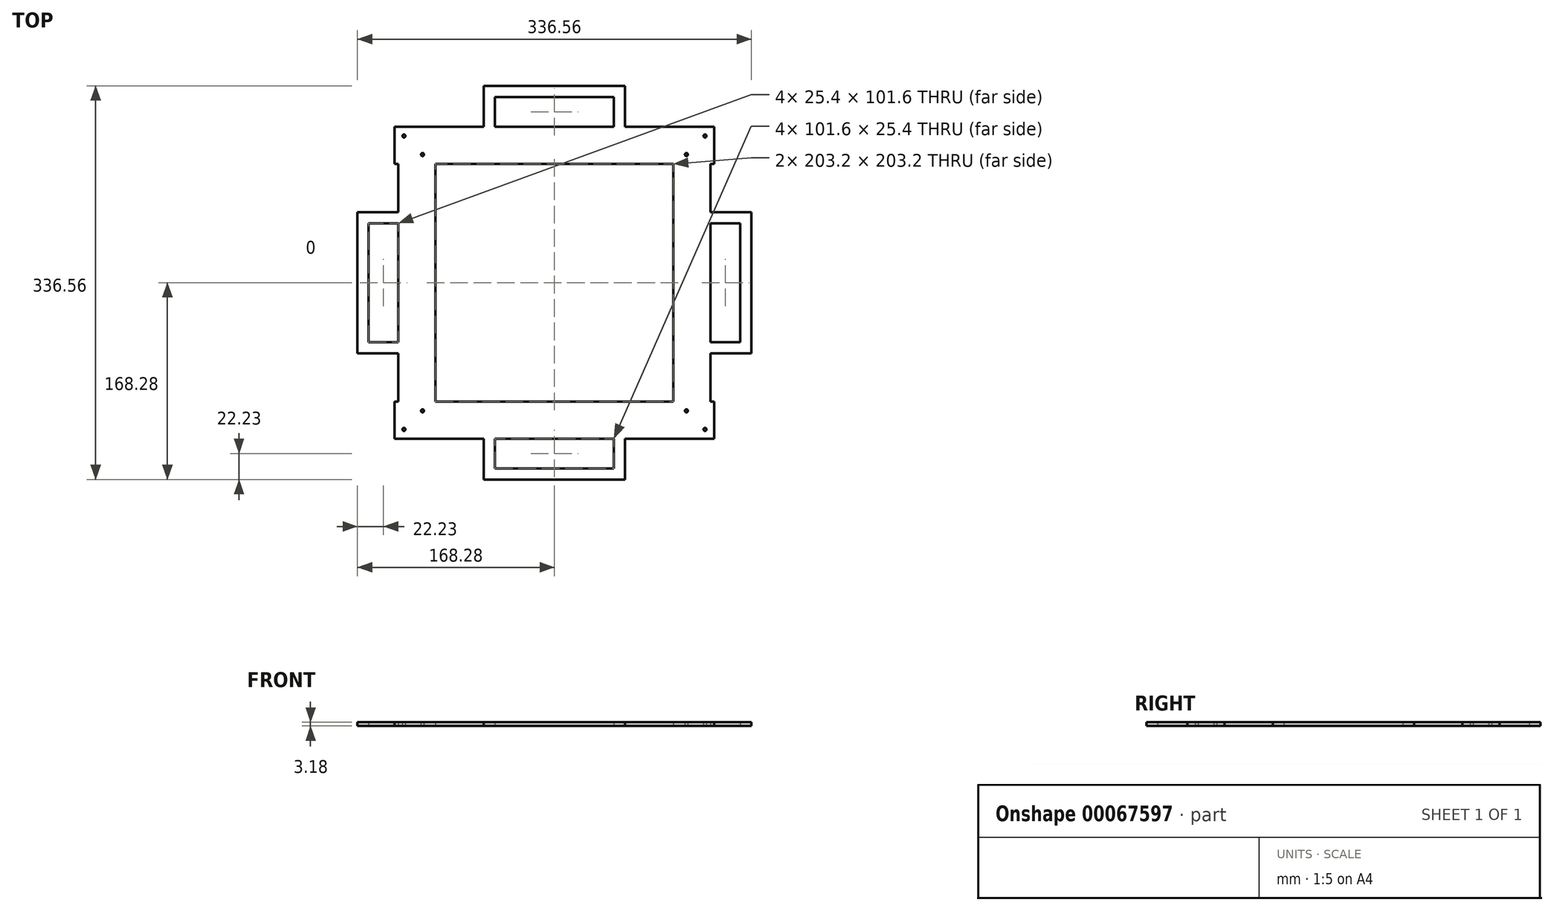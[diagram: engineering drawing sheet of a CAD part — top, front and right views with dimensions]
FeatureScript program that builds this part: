
annotation { "Feature Type Name" : "Feature", "Feature Type Description" : "" }
export const myFeature = defineFeature(function(context is Context, id is Id, definition is map)
    precondition{}
    {
        {
            var Q0;
            Q0=qCreatedBy(makeId("Top.planeOp"),FACE);
            var sketch = newSketch(context, id + "F0", { "sketchPlane" : qUnion([Q0])});
            skLineSegment(sketch, "E0.rect.bottom", {"start": v(101.6, 101.6) * mm, "end": v(-101.6, 101.6) * mm});
            skLineSegment(sketch, "E0.rect.top", {"start": v(101.6, -101.6) * mm, "end": v(-101.6, -101.6) * mm});
            skLineSegment(sketch, "E0.rect.left", {"start": v(101.6, 101.6) * mm, "end": v(101.6, -101.6) * mm});
            skLineSegment(sketch, "E0.rect.right", {"start": v(-101.6, 101.6) * mm, "end": v(-101.6, -101.6) * mm});
            skPoint(sketch, "E0.rect.middle", {"position": v(0, 0) * mm});
            skLineSegment(sketch, "E1", {"start": v(-101.6, 101.6) * mm, "end": v(-104.78, 101.6) * mm});
            skLineSegment(sketch, "E2", {"start": v(101.6, 101.6) * mm, "end": v(104.78, 101.6) * mm});
            skLineSegment(sketch, "E3.0", {"start": v(-133.35, 101.6) * mm, "end": v(-133.35, -101.6) * mm});
            skLineSegment(sketch, "E4", {"start": v(0, 101.6) * mm, "end": v(0, -101.6) * mm});
            skLineSegment(sketch, "E5.0", {"start": v(101.6, 133.35) * mm, "end": v(104.78, 133.35) * mm});
            skLineSegment(sketch, "E5.2", {"start": v(-101.6, 133.35) * mm, "end": v(-104.78, 133.35) * mm});
            skLineSegment(sketch, "E6", {"start": v(101.6, 0) * mm, "end": v(-101.6, 0) * mm});
            skLineSegment(sketch, "E7.bottom", {"start": v(-133.35, 101.6) * mm, "end": v(-136.53, 101.6) * mm});
            skLineSegment(sketch, "E7.top", {"start": v(-104.78, 133.35) * mm, "end": v(-136.53, 133.35) * mm});
            skLineSegment(sketch, "E7.left", {"start": v(-104.78, 101.6) * mm, "end": v(-104.78, 133.35) * mm});
            skLineSegment(sketch, "E7.right", {"start": v(-136.53, 101.6) * mm, "end": v(-136.53, 133.35) * mm});
            skLineSegment(sketch, "E8", {"start": v(-104.78, 101.6) * mm, "end": v(-120.65, 117.48) * mm});
            skLineSegment(sketch, "E9", {"start": v(-120.65, 117.48) * mm, "end": v(-136.53, 133.35) * mm});
            skCircle(sketch, "E10", {"center": v(-128.59, 125.41) * mm, "radius": 1.26 * mm});
            skCircle(sketch, "E11", {"center": v(-112.71, 109.54) * mm, "radius": 1.26 * mm});
            skLineSegment(sketch, "E12.MirrorCS", {"start": v(133.35, 101.6) * mm, "end": v(136.53, 101.6) * mm});
            skLineSegment(sketch, "E13.MirrorCS", {"start": v(136.53, 101.6) * mm, "end": v(136.53, 133.35) * mm});
            skLineSegment(sketch, "E14.MirrorCS", {"start": v(104.78, 133.35) * mm, "end": v(136.53, 133.35) * mm});
            skCircle(sketch, "E15.MirrorC", {"center": v(112.71, -109.54) * mm, "radius": 1.26 * mm});
            skCircle(sketch, "E16.MirrorC", {"center": v(128.59, -125.41) * mm, "radius": 1.26 * mm});
            skLineSegment(sketch, "E17.MirrorCS", {"start": v(136.53, -101.6) * mm, "end": v(136.53, -133.35) * mm});
            skLineSegment(sketch, "E18.MirrorCS", {"start": v(133.35, -101.6) * mm, "end": v(136.53, -101.6) * mm});
            skLineSegment(sketch, "E19.MirrorCS", {"start": v(-133.35, -101.6) * mm, "end": v(-136.53, -101.6) * mm});
            skLineSegment(sketch, "E20.MirrorCS", {"start": v(-136.53, -101.6) * mm, "end": v(-136.53, -133.35) * mm});
            skLineSegment(sketch, "E21", {"start": v(101.6, 133.35) * mm, "end": v(-101.6, 133.35) * mm});
            skLineSegment(sketch, "E22", {"start": v(133.35, 101.6) * mm, "end": v(133.35, -101.6) * mm});
            skLineSegment(sketch, "E23", {"start": v(136.53, -133.35) * mm, "end": v(-136.53, -133.35) * mm});
            skLineSegment(sketch, "E24", {"start": v(0, 133.35) * mm, "end": v(0, 158.75) * mm});
            skLineSegment(sketch, "E25", {"start": v(-50.8, 158.75) * mm, "end": v(0, 158.75) * mm});
            skLineSegment(sketch, "E26", {"start": v(0, 158.75) * mm, "end": v(50.8, 158.75) * mm});
            skLineSegment(sketch, "E27", {"start": v(50.8, 158.75) * mm, "end": v(50.8, 133.35) * mm});
            skLineSegment(sketch, "E28", {"start": v(-50.8, 158.75) * mm, "end": v(-50.8, 133.35) * mm});
            skLineSegment(sketch, "E29.0", {"start": v(-60.33, 168.28) * mm, "end": v(-60.33, 133.35) * mm});
            skLineSegment(sketch, "E29.1", {"start": v(-60.33, 168.28) * mm, "end": v(0, 168.28) * mm});
            skLineSegment(sketch, "E29.2", {"start": v(0, 168.28) * mm, "end": v(60.32, 168.28) * mm});
            skLineSegment(sketch, "E29.3", {"start": v(60.32, 168.28) * mm, "end": v(60.32, 133.35) * mm});
            skLineSegment(sketch, "E30", {"start": v(133.35, 0) * mm, "end": v(158.75, 0) * mm});
            skPoint(sketch, "E30.endSnap0", {"position": v(133.35, 0) * mm});
            skLineSegment(sketch, "E31", {"start": v(158.75, 0) * mm, "end": v(158.75, 50.8) * mm});
            skLineSegment(sketch, "E32", {"start": v(158.75, 50.8) * mm, "end": v(133.35, 50.8) * mm});
            skLineSegment(sketch, "E33.0", {"start": v(168.28, 60.33) * mm, "end": v(133.35, 60.33) * mm});
            skLineSegment(sketch, "E33.1", {"start": v(168.28, 0) * mm, "end": v(168.28, 60.33) * mm});
            skLineSegment(sketch, "E34.MirrorCS", {"start": v(158.75, -50.8) * mm, "end": v(133.35, -50.8) * mm});
            skLineSegment(sketch, "E35.MirrorCS", {"start": v(168.28, -60.33) * mm, "end": v(133.35, -60.33) * mm});
            skLineSegment(sketch, "E36.MirrorCS", {"start": v(168.28, 0) * mm, "end": v(168.28, -60.33) * mm});
            skLineSegment(sketch, "E37.MirrorCS", {"start": v(158.75, 0) * mm, "end": v(158.75, -50.8) * mm});
            skLineSegment(sketch, "E38.MirrorCS", {"start": v(-50.8, -158.75) * mm, "end": v(0, -158.75) * mm});
            skLineSegment(sketch, "E39.MirrorCS", {"start": v(0, -158.75) * mm, "end": v(50.8, -158.75) * mm});
            skLineSegment(sketch, "E40.MirrorCS", {"start": v(50.8, -158.75) * mm, "end": v(50.8, -133.35) * mm});
            skLineSegment(sketch, "E41.MirrorCS", {"start": v(60.32, -168.28) * mm, "end": v(60.32, -133.35) * mm});
            skLineSegment(sketch, "E42.MirrorCS", {"start": v(0, -168.28) * mm, "end": v(60.32, -168.28) * mm});
            skLineSegment(sketch, "E43.MirrorCS", {"start": v(-60.33, -168.28) * mm, "end": v(0, -168.28) * mm});
            skLineSegment(sketch, "E44.MirrorCS", {"start": v(-60.33, -168.28) * mm, "end": v(-60.33, -133.35) * mm});
            skLineSegment(sketch, "E45.MirrorCS", {"start": v(-50.8, -158.75) * mm, "end": v(-50.8, -133.35) * mm});
            skLineSegment(sketch, "E46.MirrorCS", {"start": v(0, -101.6) * mm, "end": v(0, 101.6) * mm});
            skLineSegment(sketch, "E47.MirrorCS", {"start": v(-168.28, 60.33) * mm, "end": v(-133.35, 60.33) * mm});
            skLineSegment(sketch, "E48.MirrorCS", {"start": v(-158.75, 50.8) * mm, "end": v(-133.35, 50.8) * mm});
            skLineSegment(sketch, "E49.MirrorCS", {"start": v(-158.75, 0) * mm, "end": v(-158.75, 50.8) * mm});
            skLineSegment(sketch, "E50.MirrorCS", {"start": v(-168.28, 0) * mm, "end": v(-168.28, 60.33) * mm});
            skLineSegment(sketch, "E51.MirrorCS", {"start": v(-158.75, 0) * mm, "end": v(-158.75, -50.8) * mm});
            skLineSegment(sketch, "E52.MirrorCS", {"start": v(-168.28, 0) * mm, "end": v(-168.28, -60.33) * mm});
            skLineSegment(sketch, "E53.MirrorCS", {"start": v(-168.28, -60.33) * mm, "end": v(-133.35, -60.33) * mm});
            skLineSegment(sketch, "E54.MirrorCS", {"start": v(-158.75, -50.8) * mm, "end": v(-133.35, -50.8) * mm});
            skCircle(sketch, "E55.MirrorC", {"center": v(112.71, 109.54) * mm, "radius": 1.26 * mm});
            skCircle(sketch, "E56.MirrorC", {"center": v(128.59, 125.41) * mm, "radius": 1.26 * mm});
            skCircle(sketch, "E57.MirrorC", {"center": v(-112.71, -109.54) * mm, "radius": 1.26 * mm});
            skCircle(sketch, "E58.MirrorC", {"center": v(-128.59, -125.41) * mm, "radius": 1.26 * mm});
            skSolve(sketch);
        }
        {
            var Q0;
            Q0 = qSketchRegion(id + "F0", true);
            extrude(context, id + "F1", {"entities" : qUnion([Q0]), "depth" : 3.17 * mm});
        }
    });
